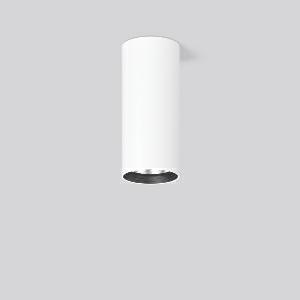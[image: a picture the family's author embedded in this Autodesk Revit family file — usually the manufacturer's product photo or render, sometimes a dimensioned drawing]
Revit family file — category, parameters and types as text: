
# Revit family: heledon_mini_a_931201_002_3_5800
name_source: partatom
category: Lighting Fixtures
units: mm (PartAtom-declared; Revit-internal decimal feet)

## family parameters
Cut with Voids When Loaded = No
Host = Face
Light Source = No
Part Type = Normal
Room Calculation Point = No
Round Connector Dimension = Use Diameter
Shared = No

## types (1)
- HELEDON mini A (1 x LED Modul 935, 2500 lm, 3500)
    Apparent Load = 20 VA
    Approval mark = CE
    CIE Flux Codes = 99 100 100 100 100
    Color Rendering = 92
    Color Temperature = 3500
    Default Elevation = 1800 mm
    Description = Series: HELEDON mini
Cylindrical surface-mounted downlight. Housing: die-cast aluminium, powder-coated. Internal ceiling frame polycarbonate with bayonet mounting. Black plastic ring and recessed LED to prevent glare from the side. Optical assembly with reflector made of MIRO-Silver with 98% total light reflection for outstanding efficiency - can be changed without tools. Best colour rendering index Ra>90. Suitable for Ceiling mounting. Easy installation with a separate ceiling frame with bayonet mounting and plug connection. Driver integrated. Connected via plug-in connector. High quality converter without flickering and stroboscopic effect. The following accessories can be mounted without use of tools: interchangeable lenses, decorative glasses, honeycomb louvre, clear and frosted diffusers, white interchangeable plastic ring. 
Colour: traffic white, matt (RAL 9016)
Diameter: 87 mm
Height: 197 mm
Lamp: LED
Socket: without socket
Colour temperature: 3500K
Colour rendering index (CRI): 92
System power: 20 W
Rated luminous flux: 2500 lm
Luminous efficiency: 125 lm/W
Control gear: Regulated power supply
Protection class: I
Type of protection: IP 20
    Height = 197 mm
    Lamp = 1 x LED Modul 935
    Lamp Light Flux = 2500 lm
    Lamp count = 1
    Length = 87 mm
    Lifetime = 50000 h
    Luminous efficacy = 125 lm/W
    Manufacturer = RZB
    ModVariant = No
    Model = 931201.002.3
    Mounting Place = Ceiling
    Mounting Type = Surface mounted
    Number of Poles = 1
    OnlyDefault = Yes
    Power Factor = 1
    Product Name = HELEDON mini A
    Product group = Surface mounted downlights
    ProductGroupID = 302
    Protection Class = Protection class I
    Protection Degree = IP 20
    RLX_Detail_Level = 1
    RLX_Emergency_Light_Flux = 0 lm
    RLX_Emergency_Type = 0
    RLX_Emergency_Type_DB = No
    RlxData = <blob elided: 107773 chars, md5=43f67807>
    Socket = socket
    Standby Power = 0 W
    System Light Flux = 2500 lm
    System Power = 20 W
    Type Comments = Product without accessories
    Type Image = 931188.002.jpg
    URL = http://relux.com
    VarID = ---
    Voltage = 230 V
    Voltage Range = 220-240 V
    Weight = 0.00 kg
    Width = 0 mm  [stored 0 ft]

note: [stored X ft] marks values corroborated as IEEE doubles in the binary element streams (Revit-internal decimal feet)

## geometry (parser evidence)
native form markers: Blend x4, Sweep x10
no freeform markers — native parametric forms only
